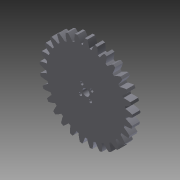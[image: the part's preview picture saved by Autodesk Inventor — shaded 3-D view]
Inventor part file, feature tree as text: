
AUTODESK INVENTOR PART (.ipt)
format: ipt  version: 2015 (Build 190159000, 159)  size: 252,416 bytes
history: native  units: mm (DEFAULTED — no unit token found)
features: plane x3, other x3, sketch x3, extrude x2
ambient origin geometry x8: Origin, YZ Plane, XZ Plane, XY Plane, X Axis, Y Axis, Z Axis, Center Point
bodies: Solid1 (feature_tree)
feature tree (11):
  extrude  "Extrusion1"  Depth=8.89mm TaperAngle=0.0deg
  plane  "Work Plane1"
  plane  "Work Plane2"
  plane  "Work Plane3"
  other  "Spur Gear"
  extrude  "Extrusion2"  Depth=76.2mm TaperAngle=0.0deg
  sketch  "Sketch1"  dims[d0=104.986667mm d1=8.89mm d2=0.0mm]
  sketch  "Sketch2"  dims[d3=98.213333mm d4=76.2mm d5=0.0mm]
  other  "Srf1"
  sketch  "Sketch3"  dims[d6=0.0mm d7=1.083308mm d9=0.0mm d14=0.0mm d15=96.52mm d16=0.0mm d17=0.0mm d18=0.0mm d19=96.52mm d20=25.4mm d21=0.0mm]
  other  "Pitch Diameter"
